# Revit family: Shingles-Section
name_source: partatom
category: Detail Items
revit_build: Autodesk Revit Architecture 2012 (Build: 20110210_1515)
units: mm (PartAtom-declared; Revit-internal decimal feet)

## types (11) — shared parameters

## per-type parameters (varying)
| type | Exposure | Keynote | Length | Taper End | Taper Start |
| 12" Asphalt Shingle | 0' - 5" | 07 31 00.A1 | 1' - 0" | 0' - 0 1/8" | 0' - 0 1/8" |
| 13 3/4" Laminated Shingle | 0' - 5 7/8" | 07 31 00.H3 | 1' - 1 3/4" | 0' - 0 1/16" | 0' - 0 1/8" |
| 13 3/8" Laminated Shingle | 0' - 5" | 07 31 00.H2 | 1' - 1 3/8" | 0' - 0 1/16" | 0' - 0 1/8" |
| 13 1/4" Laminated Shingle | 0' - 3 3/4" | 07 31 00.H1 | 1' - 1 1/4" | 0' - 0 1/16" | 0' - 0 1/8" |
| 16" Wood Shingle | 0' - 5" | 07 31 00.H6 | 1' - 4" | 0' - 0 1/4" | 0' - 0 3/8" |
| 18" Wood Shingle | 0' - 5 1/2" | 07 31 00.H7 | 1' - 6" | 0' - 0 1/4" | 0' - 0 3/8" |
| 24" Wood Shingle | 0' - 7 1/2" | 07 31 00.H8 | 2' - 0" | 0' - 0 1/4" | 0' - 0 3/8" |
| 18" Medium Wood Shake | 0' - 7 1/2" | 07 31 00.J1 | 1' - 6" | 0' - 0 1/4" | 0' - 0 1/2" |
| 24" Medium Wood Shake | 0' - 10" | 07 31 00.J2 | 2' - 0" | 0' - 0 1/4" | 0' - 0 1/2" |
| 18" Heavy Wood Shake | 0' - 7 1/2" | 07 31 00.J3 | 1' - 6" | 0' - 0 1/4" | 0' - 0 3/4" |
| 24" Heavy Wood Shake | 0' - 10" | 07 31 00.J4 | 2' - 0" | 0' - 0 1/4" | 0' - 0 3/4" |

## geometry (parser evidence)
native form markers: Sweep x1
no freeform markers — native parametric forms only
